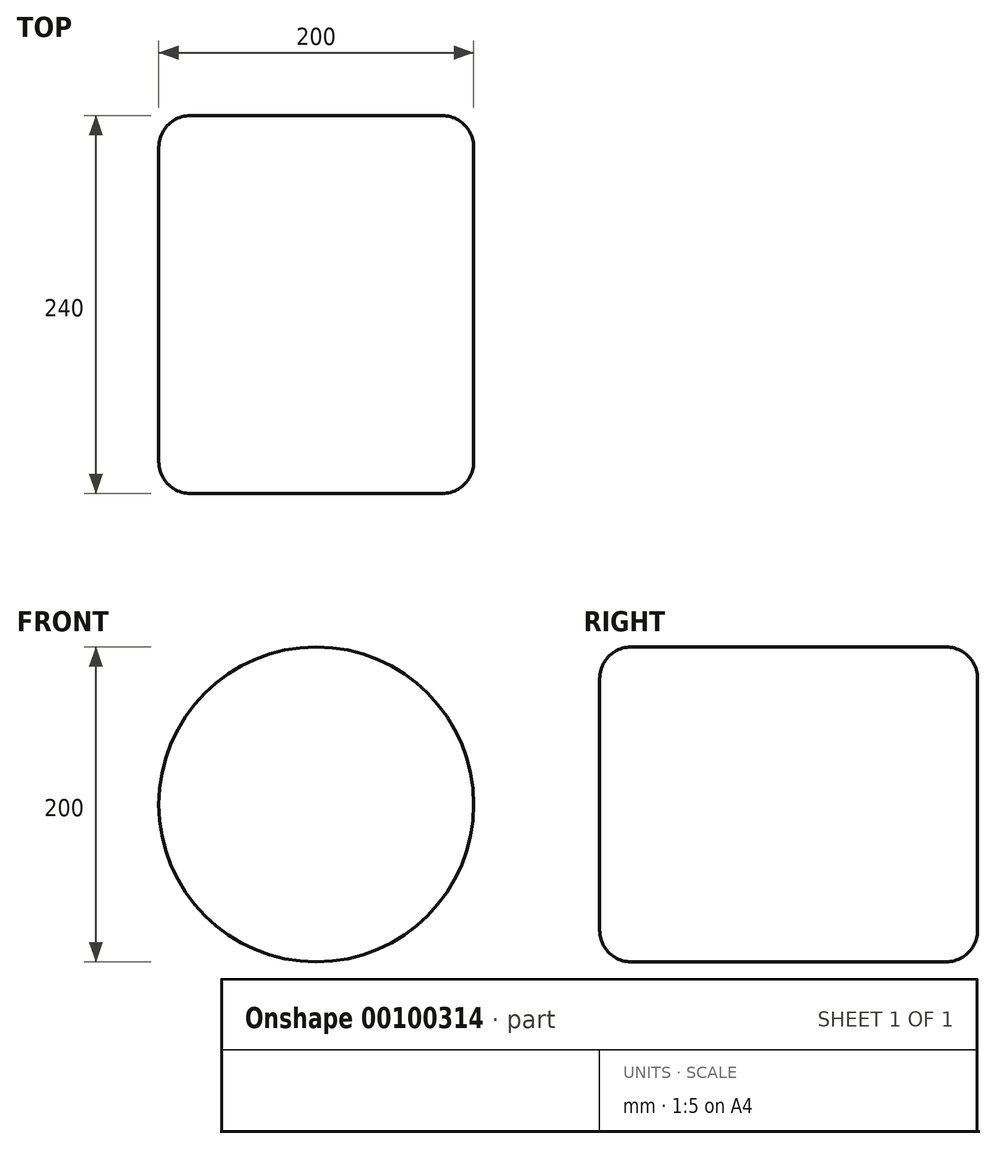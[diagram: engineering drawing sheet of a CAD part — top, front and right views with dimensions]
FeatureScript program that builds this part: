
annotation { "Feature Type Name" : "Feature", "Feature Type Description" : "" }
export const myFeature = defineFeature(function(context is Context, id is Id, definition is map)
    precondition{}
    {
        {
            var Q0;
            Q0=qCreatedBy(makeId("Front.planeOp"),FACE);
            var sketch = newSketch(context, id + "F0", { "sketchPlane" : qUnion([Q0])});
            skCircle(sketch, "E0", {"center": v(0, 0) * mm, "radius": 100 * mm});
            skSolve(sketch);
        }
        {
            var Q0;
            Q0=makeQuery(id+"F0.imprint","IMPRINT",FACE,{"disambiguationData":[TD([[makeQuery(id+"F0.imprint","IMPRINT",EDGE,{"derivedFrom":sQuery(id+"F0.wireOp",EDGE,"E0")}),1.0]])]});
            extrude(context, id + "F1", {"entities" : qUnion([Q0]), "depth" : 120 * mm});
        }
        {
            var Q0;
            Q0=makeQuery(id+"F1.opExtrude","CAP_EDGE",EDGE,{"disambiguationData":[OSD([sQuery(id+"F0.wireOp",EDGE,"E0")])],"isStart":false});
            fillet(context, id + "F2", {"entities" : qUnion([Q0]), "radius" : 20 * mm, "tangentPropagation" : true, "allowEdgeOverflow" : false});
        }
        {
            var Q0;
            Q0=makeQuery(id+"F1.opExtrude","SWEPT_BODY",BODY,{"disambiguationData":[OSD([sQuery(id+"F0.wireOp",EDGE,"E0")])]});
            var Q1;
            Q1=makeQuery(id+"F1.opExtrude","CAP_FACE",FACE,{"disambiguationData":[OSD([sQuery(id+"F0.wireOp",EDGE,"E0")])],"isStart":true});
            mirror(context, id + "F3", {"operationType" : NewBodyOperationType.ADD, "entities" : qUnion([Q0]), "mirrorPlane" : qUnion([Q1])});
        }
    });
